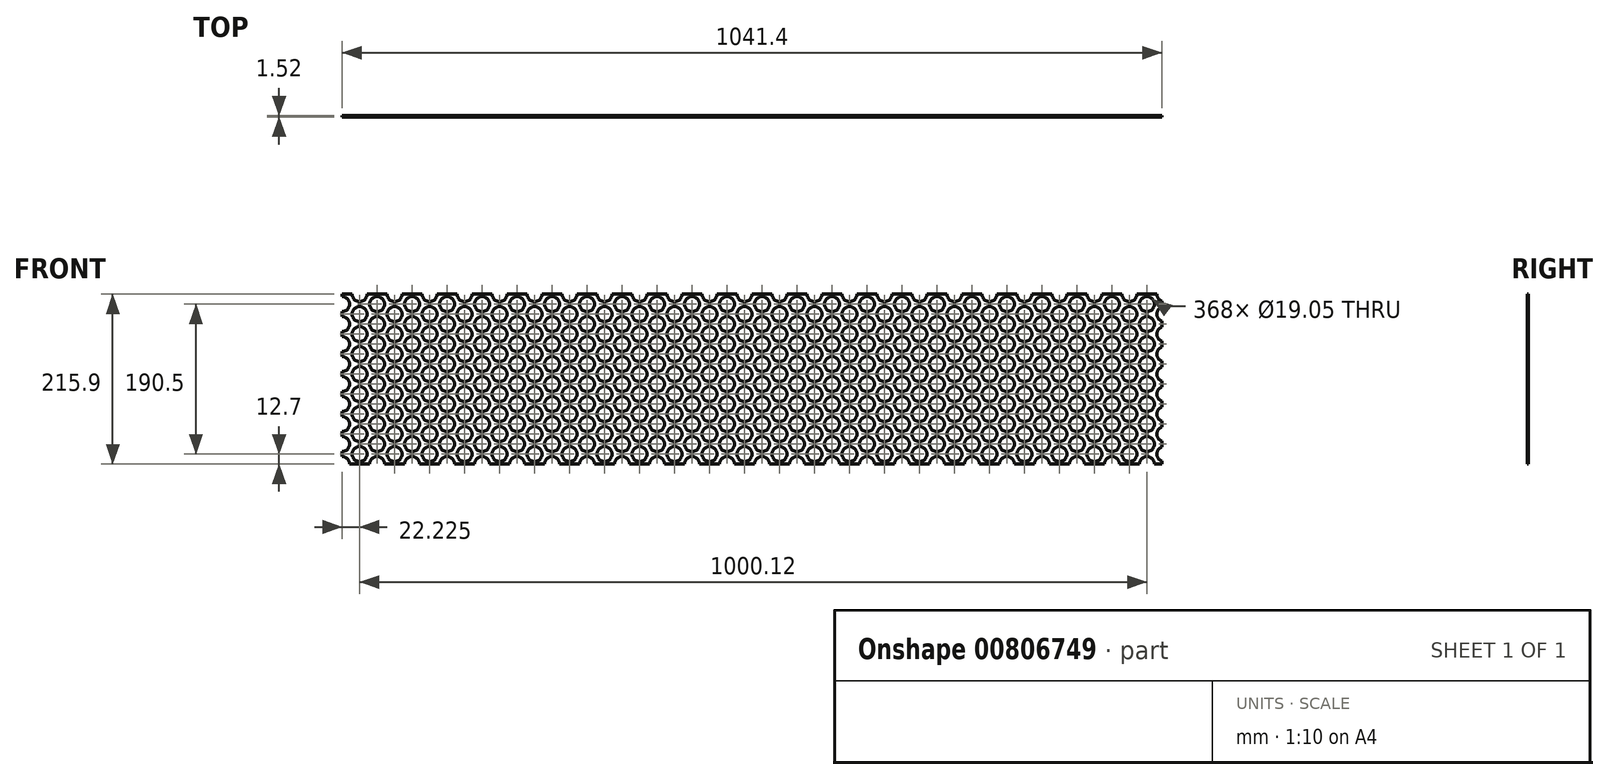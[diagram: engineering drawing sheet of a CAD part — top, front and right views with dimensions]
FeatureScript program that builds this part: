
annotation { "Feature Type Name" : "Feature", "Feature Type Description" : "" }
export const myFeature = defineFeature(function(context is Context, id is Id, definition is map)
    precondition{}
    {
        {
            var Q0;
            Q0=qCreatedBy(makeId("Front.planeOp"),FACE);
            var sketch = newSketch(context, id + "F0", { "sketchPlane" : qUnion([Q0])});
            skLineSegment(sketch, "E0.bottom", {"start": v(0, 0) * mm, "end": v(1041.4, 0) * mm});
            skLineSegment(sketch, "E0.top", {"start": v(0, 215.9) * mm, "end": v(1041.4, 215.9) * mm});
            skLineSegment(sketch, "E0.left", {"start": v(0, 0) * mm, "end": v(0, 215.9) * mm});
            skLineSegment(sketch, "E0.right", {"start": v(1041.4, 0) * mm, "end": v(1041.4, 215.9) * mm});
            skSolve(sketch);
        }
        {
            var Q0;
            Q0 = qSketchRegion(id + "F0", true);
            extrude(context, id + "F1", {"entities" : qUnion([Q0]), "depth" : 1.52 * mm, "offsetDistance" : 25.4 * mm});
        }
        {
            var Q0;
            Q0=makeQuery(id+"F1.opExtrude","CAP_FACE",FACE,{"disambiguationData":[OSD([sQuery(id+"F0.wireOp",EDGE,"E0.bottom"),sQuery(id+"F0.wireOp",EDGE,"E0.top"),sQuery(id+"F0.wireOp",EDGE,"E0.left"),sQuery(id+"F0.wireOp",EDGE,"E0.right")])],"isStart":false});
            var sketch = newSketch(context, id + "F2", { "sketchPlane" : qUnion([Q0])});
            skCircle(sketch, "E1", {"center": v(0, 0) * mm, "radius": 9.53 * mm});
            skCircle(sketch, "E2.0.1.0", {"center": v(0, 25.4) * mm, "radius": 9.53 * mm});
            skCircle(sketch, "E2.0.2.0", {"center": v(0, 50.8) * mm, "radius": 9.53 * mm});
            skCircle(sketch, "E2.0.3.0", {"center": v(0, 76.2) * mm, "radius": 9.53 * mm});
            skCircle(sketch, "E2.0.4.0", {"center": v(0, 101.6) * mm, "radius": 9.53 * mm});
            skCircle(sketch, "E2.0.5.0", {"center": v(0, 127) * mm, "radius": 9.53 * mm});
            skCircle(sketch, "E2.0.6.0", {"center": v(0, 152.4) * mm, "radius": 9.53 * mm});
            skCircle(sketch, "E2.0.7.0", {"center": v(0, 177.8) * mm, "radius": 9.53 * mm});
            skCircle(sketch, "E2.0.8.0", {"center": v(0, 203.2) * mm, "radius": 9.53 * mm});
            skCircle(sketch, "E2.1.0.0", {"center": v(44.45, 0) * mm, "radius": 9.53 * mm});
            skCircle(sketch, "E2.1.1.0", {"center": v(44.45, 25.4) * mm, "radius": 9.53 * mm});
            skCircle(sketch, "E2.1.2.0", {"center": v(44.45, 50.8) * mm, "radius": 9.53 * mm});
            skCircle(sketch, "E2.1.3.0", {"center": v(44.45, 76.2) * mm, "radius": 9.53 * mm});
            skCircle(sketch, "E2.1.4.0", {"center": v(44.45, 101.6) * mm, "radius": 9.53 * mm});
            skCircle(sketch, "E2.1.5.0", {"center": v(44.45, 127) * mm, "radius": 9.53 * mm});
            skCircle(sketch, "E2.1.6.0", {"center": v(44.45, 152.4) * mm, "radius": 9.53 * mm});
            skCircle(sketch, "E2.1.7.0", {"center": v(44.45, 177.8) * mm, "radius": 9.53 * mm});
            skCircle(sketch, "E2.1.8.0", {"center": v(44.45, 203.2) * mm, "radius": 9.53 * mm});
            skCircle(sketch, "E2.2.0.0", {"center": v(88.9, 0) * mm, "radius": 9.53 * mm});
            skCircle(sketch, "E2.2.1.0", {"center": v(88.9, 25.4) * mm, "radius": 9.53 * mm});
            skCircle(sketch, "E2.2.2.0", {"center": v(88.9, 50.8) * mm, "radius": 9.53 * mm});
            skCircle(sketch, "E2.2.3.0", {"center": v(88.9, 76.2) * mm, "radius": 9.53 * mm});
            skCircle(sketch, "E2.2.4.0", {"center": v(88.9, 101.6) * mm, "radius": 9.53 * mm});
            skCircle(sketch, "E2.2.5.0", {"center": v(88.9, 127) * mm, "radius": 9.53 * mm});
            skCircle(sketch, "E2.2.6.0", {"center": v(88.9, 152.4) * mm, "radius": 9.53 * mm});
            skCircle(sketch, "E2.2.7.0", {"center": v(88.9, 177.8) * mm, "radius": 9.53 * mm});
            skCircle(sketch, "E2.2.8.0", {"center": v(88.9, 203.2) * mm, "radius": 9.53 * mm});
            skCircle(sketch, "E2.3.0.0", {"center": v(133.35, 0) * mm, "radius": 9.53 * mm});
            skCircle(sketch, "E2.3.1.0", {"center": v(133.35, 25.4) * mm, "radius": 9.53 * mm});
            skCircle(sketch, "E2.3.2.0", {"center": v(133.35, 50.8) * mm, "radius": 9.53 * mm});
            skCircle(sketch, "E2.3.3.0", {"center": v(133.35, 76.2) * mm, "radius": 9.53 * mm});
            skCircle(sketch, "E2.3.4.0", {"center": v(133.35, 101.6) * mm, "radius": 9.53 * mm});
            skCircle(sketch, "E2.3.5.0", {"center": v(133.35, 127) * mm, "radius": 9.53 * mm});
            skCircle(sketch, "E2.3.6.0", {"center": v(133.35, 152.4) * mm, "radius": 9.53 * mm});
            skCircle(sketch, "E2.3.7.0", {"center": v(133.35, 177.8) * mm, "radius": 9.53 * mm});
            skCircle(sketch, "E2.3.8.0", {"center": v(133.35, 203.2) * mm, "radius": 9.53 * mm});
            skCircle(sketch, "E2.4.0.0", {"center": v(177.8, 0) * mm, "radius": 9.53 * mm});
            skCircle(sketch, "E2.4.1.0", {"center": v(177.8, 25.4) * mm, "radius": 9.53 * mm});
            skCircle(sketch, "E2.4.2.0", {"center": v(177.8, 50.8) * mm, "radius": 9.53 * mm});
            skCircle(sketch, "E2.4.3.0", {"center": v(177.8, 76.2) * mm, "radius": 9.53 * mm});
            skCircle(sketch, "E2.4.4.0", {"center": v(177.8, 101.6) * mm, "radius": 9.53 * mm});
            skCircle(sketch, "E2.4.5.0", {"center": v(177.8, 127) * mm, "radius": 9.53 * mm});
            skCircle(sketch, "E2.4.6.0", {"center": v(177.8, 152.4) * mm, "radius": 9.53 * mm});
            skCircle(sketch, "E2.4.7.0", {"center": v(177.8, 177.8) * mm, "radius": 9.53 * mm});
            skCircle(sketch, "E2.4.8.0", {"center": v(177.8, 203.2) * mm, "radius": 9.53 * mm});
            skCircle(sketch, "E2.5.0.0", {"center": v(222.25, 0) * mm, "radius": 9.53 * mm});
            skCircle(sketch, "E2.5.1.0", {"center": v(222.25, 25.4) * mm, "radius": 9.53 * mm});
            skCircle(sketch, "E2.5.2.0", {"center": v(222.25, 50.8) * mm, "radius": 9.53 * mm});
            skCircle(sketch, "E2.5.3.0", {"center": v(222.25, 76.2) * mm, "radius": 9.53 * mm});
            skCircle(sketch, "E2.5.4.0", {"center": v(222.25, 101.6) * mm, "radius": 9.53 * mm});
            skCircle(sketch, "E2.5.5.0", {"center": v(222.25, 127) * mm, "radius": 9.53 * mm});
            skCircle(sketch, "E2.5.6.0", {"center": v(222.25, 152.4) * mm, "radius": 9.53 * mm});
            skCircle(sketch, "E2.5.7.0", {"center": v(222.25, 177.8) * mm, "radius": 9.53 * mm});
            skCircle(sketch, "E2.5.8.0", {"center": v(222.25, 203.2) * mm, "radius": 9.53 * mm});
            skCircle(sketch, "E2.6.0.0", {"center": v(266.7, 0) * mm, "radius": 9.53 * mm});
            skCircle(sketch, "E2.6.1.0", {"center": v(266.7, 25.4) * mm, "radius": 9.53 * mm});
            skCircle(sketch, "E2.6.2.0", {"center": v(266.7, 50.8) * mm, "radius": 9.53 * mm});
            skCircle(sketch, "E2.6.3.0", {"center": v(266.7, 76.2) * mm, "radius": 9.53 * mm});
            skCircle(sketch, "E2.6.4.0", {"center": v(266.7, 101.6) * mm, "radius": 9.53 * mm});
            skCircle(sketch, "E2.6.5.0", {"center": v(266.7, 127) * mm, "radius": 9.53 * mm});
            skCircle(sketch, "E2.6.6.0", {"center": v(266.7, 152.4) * mm, "radius": 9.53 * mm});
            skCircle(sketch, "E2.6.7.0", {"center": v(266.7, 177.8) * mm, "radius": 9.53 * mm});
            skCircle(sketch, "E2.6.8.0", {"center": v(266.7, 203.2) * mm, "radius": 9.53 * mm});
            skCircle(sketch, "E2.7.0.0", {"center": v(311.15, 0) * mm, "radius": 9.53 * mm});
            skCircle(sketch, "E2.7.1.0", {"center": v(311.15, 25.4) * mm, "radius": 9.53 * mm});
            skCircle(sketch, "E2.7.2.0", {"center": v(311.15, 50.8) * mm, "radius": 9.53 * mm});
            skCircle(sketch, "E2.7.3.0", {"center": v(311.15, 76.2) * mm, "radius": 9.53 * mm});
            skCircle(sketch, "E2.7.4.0", {"center": v(311.15, 101.6) * mm, "radius": 9.53 * mm});
            skCircle(sketch, "E2.7.5.0", {"center": v(311.15, 127) * mm, "radius": 9.53 * mm});
            skCircle(sketch, "E2.7.6.0", {"center": v(311.15, 152.4) * mm, "radius": 9.53 * mm});
            skCircle(sketch, "E2.7.7.0", {"center": v(311.15, 177.8) * mm, "radius": 9.53 * mm});
            skCircle(sketch, "E2.7.8.0", {"center": v(311.15, 203.2) * mm, "radius": 9.53 * mm});
            skCircle(sketch, "E2.8.0.0", {"center": v(355.6, 0) * mm, "radius": 9.53 * mm});
            skCircle(sketch, "E2.8.1.0", {"center": v(355.6, 25.4) * mm, "radius": 9.53 * mm});
            skCircle(sketch, "E2.8.2.0", {"center": v(355.6, 50.8) * mm, "radius": 9.53 * mm});
            skCircle(sketch, "E2.8.3.0", {"center": v(355.6, 76.2) * mm, "radius": 9.53 * mm});
            skCircle(sketch, "E2.8.4.0", {"center": v(355.6, 101.6) * mm, "radius": 9.53 * mm});
            skCircle(sketch, "E2.8.5.0", {"center": v(355.6, 127) * mm, "radius": 9.53 * mm});
            skCircle(sketch, "E2.8.6.0", {"center": v(355.6, 152.4) * mm, "radius": 9.53 * mm});
            skCircle(sketch, "E2.8.7.0", {"center": v(355.6, 177.8) * mm, "radius": 9.53 * mm});
            skCircle(sketch, "E2.8.8.0", {"center": v(355.6, 203.2) * mm, "radius": 9.53 * mm});
            skCircle(sketch, "E2.9.0.0", {"center": v(400.05, 0) * mm, "radius": 9.53 * mm});
            skCircle(sketch, "E2.9.1.0", {"center": v(400.05, 25.4) * mm, "radius": 9.53 * mm});
            skCircle(sketch, "E2.9.2.0", {"center": v(400.05, 50.8) * mm, "radius": 9.53 * mm});
            skCircle(sketch, "E2.9.3.0", {"center": v(400.05, 76.2) * mm, "radius": 9.53 * mm});
            skCircle(sketch, "E2.9.4.0", {"center": v(400.05, 101.6) * mm, "radius": 9.53 * mm});
            skCircle(sketch, "E2.9.5.0", {"center": v(400.05, 127) * mm, "radius": 9.53 * mm});
            skCircle(sketch, "E2.9.6.0", {"center": v(400.05, 152.4) * mm, "radius": 9.53 * mm});
            skCircle(sketch, "E2.9.7.0", {"center": v(400.05, 177.8) * mm, "radius": 9.53 * mm});
            skCircle(sketch, "E2.9.8.0", {"center": v(400.05, 203.2) * mm, "radius": 9.53 * mm});
            skCircle(sketch, "E2.10.0.0", {"center": v(444.5, 0) * mm, "radius": 9.53 * mm});
            skCircle(sketch, "E2.10.1.0", {"center": v(444.5, 25.4) * mm, "radius": 9.53 * mm});
            skCircle(sketch, "E2.10.2.0", {"center": v(444.5, 50.8) * mm, "radius": 9.53 * mm});
            skCircle(sketch, "E2.10.3.0", {"center": v(444.5, 76.2) * mm, "radius": 9.53 * mm});
            skCircle(sketch, "E2.10.4.0", {"center": v(444.5, 101.6) * mm, "radius": 9.53 * mm});
            skCircle(sketch, "E2.10.5.0", {"center": v(444.5, 127) * mm, "radius": 9.53 * mm});
            skCircle(sketch, "E2.10.6.0", {"center": v(444.5, 152.4) * mm, "radius": 9.53 * mm});
            skCircle(sketch, "E2.10.7.0", {"center": v(444.5, 177.8) * mm, "radius": 9.53 * mm});
            skCircle(sketch, "E2.10.8.0", {"center": v(444.5, 203.2) * mm, "radius": 9.53 * mm});
            skCircle(sketch, "E2.11.0.0", {"center": v(488.95, 0) * mm, "radius": 9.53 * mm});
            skCircle(sketch, "E2.11.1.0", {"center": v(488.95, 25.4) * mm, "radius": 9.53 * mm});
            skCircle(sketch, "E2.11.2.0", {"center": v(488.95, 50.8) * mm, "radius": 9.53 * mm});
            skCircle(sketch, "E2.11.3.0", {"center": v(488.95, 76.2) * mm, "radius": 9.53 * mm});
            skCircle(sketch, "E2.11.4.0", {"center": v(488.95, 101.6) * mm, "radius": 9.53 * mm});
            skCircle(sketch, "E2.11.5.0", {"center": v(488.95, 127) * mm, "radius": 9.53 * mm});
            skCircle(sketch, "E2.11.6.0", {"center": v(488.95, 152.4) * mm, "radius": 9.53 * mm});
            skCircle(sketch, "E2.11.7.0", {"center": v(488.95, 177.8) * mm, "radius": 9.53 * mm});
            skCircle(sketch, "E2.11.8.0", {"center": v(488.95, 203.2) * mm, "radius": 9.53 * mm});
            skCircle(sketch, "E2.12.0.0", {"center": v(533.4, 0) * mm, "radius": 9.53 * mm});
            skCircle(sketch, "E2.12.1.0", {"center": v(533.4, 25.4) * mm, "radius": 9.53 * mm});
            skCircle(sketch, "E2.12.2.0", {"center": v(533.4, 50.8) * mm, "radius": 9.53 * mm});
            skCircle(sketch, "E2.12.3.0", {"center": v(533.4, 76.2) * mm, "radius": 9.53 * mm});
            skCircle(sketch, "E2.12.4.0", {"center": v(533.4, 101.6) * mm, "radius": 9.53 * mm});
            skCircle(sketch, "E2.12.5.0", {"center": v(533.4, 127) * mm, "radius": 9.53 * mm});
            skCircle(sketch, "E2.12.6.0", {"center": v(533.4, 152.4) * mm, "radius": 9.53 * mm});
            skCircle(sketch, "E2.12.7.0", {"center": v(533.4, 177.8) * mm, "radius": 9.53 * mm});
            skCircle(sketch, "E2.12.8.0", {"center": v(533.4, 203.2) * mm, "radius": 9.53 * mm});
            skCircle(sketch, "E2.13.0.0", {"center": v(577.85, 0) * mm, "radius": 9.53 * mm});
            skCircle(sketch, "E2.13.1.0", {"center": v(577.85, 25.4) * mm, "radius": 9.53 * mm});
            skCircle(sketch, "E2.13.2.0", {"center": v(577.85, 50.8) * mm, "radius": 9.53 * mm});
            skCircle(sketch, "E2.13.3.0", {"center": v(577.85, 76.2) * mm, "radius": 9.53 * mm});
            skCircle(sketch, "E2.13.4.0", {"center": v(577.85, 101.6) * mm, "radius": 9.53 * mm});
            skCircle(sketch, "E2.13.5.0", {"center": v(577.85, 127) * mm, "radius": 9.53 * mm});
            skCircle(sketch, "E2.13.6.0", {"center": v(577.85, 152.4) * mm, "radius": 9.53 * mm});
            skCircle(sketch, "E2.13.7.0", {"center": v(577.85, 177.8) * mm, "radius": 9.53 * mm});
            skCircle(sketch, "E2.13.8.0", {"center": v(577.85, 203.2) * mm, "radius": 9.53 * mm});
            skCircle(sketch, "E2.14.0.0", {"center": v(622.3, 0) * mm, "radius": 9.53 * mm});
            skCircle(sketch, "E2.14.1.0", {"center": v(622.3, 25.4) * mm, "radius": 9.53 * mm});
            skCircle(sketch, "E2.14.2.0", {"center": v(622.3, 50.8) * mm, "radius": 9.53 * mm});
            skCircle(sketch, "E2.14.3.0", {"center": v(622.3, 76.2) * mm, "radius": 9.53 * mm});
            skCircle(sketch, "E2.14.4.0", {"center": v(622.3, 101.6) * mm, "radius": 9.53 * mm});
            skCircle(sketch, "E2.14.5.0", {"center": v(622.3, 127) * mm, "radius": 9.53 * mm});
            skCircle(sketch, "E2.14.6.0", {"center": v(622.3, 152.4) * mm, "radius": 9.53 * mm});
            skCircle(sketch, "E2.14.7.0", {"center": v(622.3, 177.8) * mm, "radius": 9.53 * mm});
            skCircle(sketch, "E2.14.8.0", {"center": v(622.3, 203.2) * mm, "radius": 9.53 * mm});
            skCircle(sketch, "E2.15.0.0", {"center": v(666.75, 0) * mm, "radius": 9.53 * mm});
            skCircle(sketch, "E2.15.1.0", {"center": v(666.75, 25.4) * mm, "radius": 9.53 * mm});
            skCircle(sketch, "E2.15.2.0", {"center": v(666.75, 50.8) * mm, "radius": 9.53 * mm});
            skCircle(sketch, "E2.15.3.0", {"center": v(666.75, 76.2) * mm, "radius": 9.53 * mm});
            skCircle(sketch, "E2.15.4.0", {"center": v(666.75, 101.6) * mm, "radius": 9.53 * mm});
            skCircle(sketch, "E2.15.5.0", {"center": v(666.75, 127) * mm, "radius": 9.53 * mm});
            skCircle(sketch, "E2.15.6.0", {"center": v(666.75, 152.4) * mm, "radius": 9.53 * mm});
            skCircle(sketch, "E2.15.7.0", {"center": v(666.75, 177.8) * mm, "radius": 9.53 * mm});
            skCircle(sketch, "E2.15.8.0", {"center": v(666.75, 203.2) * mm, "radius": 9.53 * mm});
            skCircle(sketch, "E2.16.0.0", {"center": v(711.2, 0) * mm, "radius": 9.53 * mm});
            skCircle(sketch, "E2.16.1.0", {"center": v(711.2, 25.4) * mm, "radius": 9.53 * mm});
            skCircle(sketch, "E2.16.2.0", {"center": v(711.2, 50.8) * mm, "radius": 9.53 * mm});
            skCircle(sketch, "E2.16.3.0", {"center": v(711.2, 76.2) * mm, "radius": 9.53 * mm});
            skCircle(sketch, "E2.16.4.0", {"center": v(711.2, 101.6) * mm, "radius": 9.53 * mm});
            skCircle(sketch, "E2.16.5.0", {"center": v(711.2, 127) * mm, "radius": 9.53 * mm});
            skCircle(sketch, "E2.16.6.0", {"center": v(711.2, 152.4) * mm, "radius": 9.53 * mm});
            skCircle(sketch, "E2.16.7.0", {"center": v(711.2, 177.8) * mm, "radius": 9.53 * mm});
            skCircle(sketch, "E2.16.8.0", {"center": v(711.2, 203.2) * mm, "radius": 9.53 * mm});
            skCircle(sketch, "E2.17.0.0", {"center": v(755.65, 0) * mm, "radius": 9.53 * mm});
            skCircle(sketch, "E2.17.1.0", {"center": v(755.65, 25.4) * mm, "radius": 9.53 * mm});
            skCircle(sketch, "E2.17.2.0", {"center": v(755.65, 50.8) * mm, "radius": 9.53 * mm});
            skCircle(sketch, "E2.17.3.0", {"center": v(755.65, 76.2) * mm, "radius": 9.53 * mm});
            skCircle(sketch, "E2.17.4.0", {"center": v(755.65, 101.6) * mm, "radius": 9.53 * mm});
            skCircle(sketch, "E2.17.5.0", {"center": v(755.65, 127) * mm, "radius": 9.53 * mm});
            skCircle(sketch, "E2.17.6.0", {"center": v(755.65, 152.4) * mm, "radius": 9.53 * mm});
            skCircle(sketch, "E2.17.7.0", {"center": v(755.65, 177.8) * mm, "radius": 9.53 * mm});
            skCircle(sketch, "E2.17.8.0", {"center": v(755.65, 203.2) * mm, "radius": 9.53 * mm});
            skCircle(sketch, "E2.18.0.0", {"center": v(800.1, 0) * mm, "radius": 9.53 * mm});
            skCircle(sketch, "E2.18.1.0", {"center": v(800.1, 25.4) * mm, "radius": 9.53 * mm});
            skCircle(sketch, "E2.18.2.0", {"center": v(800.1, 50.8) * mm, "radius": 9.53 * mm});
            skCircle(sketch, "E2.18.3.0", {"center": v(800.1, 76.2) * mm, "radius": 9.53 * mm});
            skCircle(sketch, "E2.18.4.0", {"center": v(800.1, 101.6) * mm, "radius": 9.53 * mm});
            skCircle(sketch, "E2.18.5.0", {"center": v(800.1, 127) * mm, "radius": 9.53 * mm});
            skCircle(sketch, "E2.18.6.0", {"center": v(800.1, 152.4) * mm, "radius": 9.53 * mm});
            skCircle(sketch, "E2.18.7.0", {"center": v(800.1, 177.8) * mm, "radius": 9.53 * mm});
            skCircle(sketch, "E2.18.8.0", {"center": v(800.1, 203.2) * mm, "radius": 9.53 * mm});
            skCircle(sketch, "E2.19.0.0", {"center": v(844.55, 0) * mm, "radius": 9.53 * mm});
            skCircle(sketch, "E2.19.1.0", {"center": v(844.55, 25.4) * mm, "radius": 9.53 * mm});
            skCircle(sketch, "E2.19.2.0", {"center": v(844.55, 50.8) * mm, "radius": 9.53 * mm});
            skCircle(sketch, "E2.19.3.0", {"center": v(844.55, 76.2) * mm, "radius": 9.53 * mm});
            skCircle(sketch, "E2.19.4.0", {"center": v(844.55, 101.6) * mm, "radius": 9.53 * mm});
            skCircle(sketch, "E2.19.5.0", {"center": v(844.55, 127) * mm, "radius": 9.53 * mm});
            skCircle(sketch, "E2.19.6.0", {"center": v(844.55, 152.4) * mm, "radius": 9.53 * mm});
            skCircle(sketch, "E2.19.7.0", {"center": v(844.55, 177.8) * mm, "radius": 9.53 * mm});
            skCircle(sketch, "E2.19.8.0", {"center": v(844.55, 203.2) * mm, "radius": 9.53 * mm});
            skCircle(sketch, "E2.20.0.0", {"center": v(889, 0) * mm, "radius": 9.53 * mm});
            skCircle(sketch, "E2.20.1.0", {"center": v(889, 25.4) * mm, "radius": 9.53 * mm});
            skCircle(sketch, "E2.20.2.0", {"center": v(889, 50.8) * mm, "radius": 9.53 * mm});
            skCircle(sketch, "E2.20.3.0", {"center": v(889, 76.2) * mm, "radius": 9.53 * mm});
            skCircle(sketch, "E2.20.4.0", {"center": v(889, 101.6) * mm, "radius": 9.53 * mm});
            skCircle(sketch, "E2.20.5.0", {"center": v(889, 127) * mm, "radius": 9.53 * mm});
            skCircle(sketch, "E2.20.6.0", {"center": v(889, 152.4) * mm, "radius": 9.53 * mm});
            skCircle(sketch, "E2.20.7.0", {"center": v(889, 177.8) * mm, "radius": 9.53 * mm});
            skCircle(sketch, "E2.20.8.0", {"center": v(889, 203.2) * mm, "radius": 9.53 * mm});
            skCircle(sketch, "E2.21.0.0", {"center": v(933.45, 0) * mm, "radius": 9.53 * mm});
            skCircle(sketch, "E2.21.1.0", {"center": v(933.45, 25.4) * mm, "radius": 9.53 * mm});
            skCircle(sketch, "E2.21.2.0", {"center": v(933.45, 50.8) * mm, "radius": 9.53 * mm});
            skCircle(sketch, "E2.21.3.0", {"center": v(933.45, 76.2) * mm, "radius": 9.53 * mm});
            skCircle(sketch, "E2.21.4.0", {"center": v(933.45, 101.6) * mm, "radius": 9.53 * mm});
            skCircle(sketch, "E2.21.5.0", {"center": v(933.45, 127) * mm, "radius": 9.53 * mm});
            skCircle(sketch, "E2.21.6.0", {"center": v(933.45, 152.4) * mm, "radius": 9.53 * mm});
            skCircle(sketch, "E2.21.7.0", {"center": v(933.45, 177.8) * mm, "radius": 9.53 * mm});
            skCircle(sketch, "E2.21.8.0", {"center": v(933.45, 203.2) * mm, "radius": 9.53 * mm});
            skCircle(sketch, "E2.22.0.0", {"center": v(977.9, 0) * mm, "radius": 9.53 * mm});
            skCircle(sketch, "E2.22.1.0", {"center": v(977.9, 25.4) * mm, "radius": 9.53 * mm});
            skCircle(sketch, "E2.22.2.0", {"center": v(977.9, 50.8) * mm, "radius": 9.53 * mm});
            skCircle(sketch, "E2.22.3.0", {"center": v(977.9, 76.2) * mm, "radius": 9.53 * mm});
            skCircle(sketch, "E2.22.4.0", {"center": v(977.9, 101.6) * mm, "radius": 9.53 * mm});
            skCircle(sketch, "E2.22.5.0", {"center": v(977.9, 127) * mm, "radius": 9.53 * mm});
            skCircle(sketch, "E2.22.6.0", {"center": v(977.9, 152.4) * mm, "radius": 9.53 * mm});
            skCircle(sketch, "E2.22.7.0", {"center": v(977.9, 177.8) * mm, "radius": 9.53 * mm});
            skCircle(sketch, "E2.22.8.0", {"center": v(977.9, 203.2) * mm, "radius": 9.53 * mm});
            skCircle(sketch, "E2.23.0.0", {"center": v(1022.35, 0) * mm, "radius": 9.53 * mm});
            skCircle(sketch, "E2.23.1.0", {"center": v(1022.35, 25.4) * mm, "radius": 9.53 * mm});
            skCircle(sketch, "E2.23.2.0", {"center": v(1022.35, 50.8) * mm, "radius": 9.53 * mm});
            skCircle(sketch, "E2.23.3.0", {"center": v(1022.35, 76.2) * mm, "radius": 9.53 * mm});
            skCircle(sketch, "E2.23.4.0", {"center": v(1022.35, 101.6) * mm, "radius": 9.53 * mm});
            skCircle(sketch, "E2.23.5.0", {"center": v(1022.35, 127) * mm, "radius": 9.53 * mm});
            skCircle(sketch, "E2.23.6.0", {"center": v(1022.35, 152.4) * mm, "radius": 9.53 * mm});
            skCircle(sketch, "E2.23.7.0", {"center": v(1022.35, 177.8) * mm, "radius": 9.53 * mm});
            skCircle(sketch, "E2.23.8.0", {"center": v(1022.35, 203.2) * mm, "radius": 9.53 * mm});
            skLineSegment(sketch, "E2.direction1", {"start": v(0, 0) * mm, "end": v(44.45, 0) * mm, "construction": true});
            skLineSegment(sketch, "E2.direction2", {"start": v(0, 0) * mm, "end": v(0, 25.4) * mm, "construction": true});
            skCircle(sketch, "E3", {"center": v(22.22, 12.7) * mm, "radius": 9.53 * mm});
            skCircle(sketch, "E4.0.1.0", {"center": v(22.22, 38.1) * mm, "radius": 9.53 * mm});
            skCircle(sketch, "E4.0.2.0", {"center": v(22.22, 63.5) * mm, "radius": 9.53 * mm});
            skCircle(sketch, "E4.0.3.0", {"center": v(22.22, 88.9) * mm, "radius": 9.53 * mm});
            skCircle(sketch, "E4.0.4.0", {"center": v(22.22, 114.3) * mm, "radius": 9.53 * mm});
            skCircle(sketch, "E4.0.5.0", {"center": v(22.22, 139.7) * mm, "radius": 9.53 * mm});
            skCircle(sketch, "E4.0.6.0", {"center": v(22.22, 165.1) * mm, "radius": 9.53 * mm});
            skCircle(sketch, "E4.0.7.0", {"center": v(22.22, 190.5) * mm, "radius": 9.53 * mm});
            skCircle(sketch, "E4.0.8.0", {"center": v(22.22, 215.9) * mm, "radius": 9.53 * mm});
            skCircle(sketch, "E4.1.0.0", {"center": v(66.67, 12.7) * mm, "radius": 9.53 * mm});
            skCircle(sketch, "E4.1.1.0", {"center": v(66.67, 38.1) * mm, "radius": 9.53 * mm});
            skCircle(sketch, "E4.1.2.0", {"center": v(66.67, 63.5) * mm, "radius": 9.53 * mm});
            skCircle(sketch, "E4.1.3.0", {"center": v(66.67, 88.9) * mm, "radius": 9.53 * mm});
            skCircle(sketch, "E4.1.4.0", {"center": v(66.67, 114.3) * mm, "radius": 9.53 * mm});
            skCircle(sketch, "E4.1.5.0", {"center": v(66.67, 139.7) * mm, "radius": 9.53 * mm});
            skCircle(sketch, "E4.1.6.0", {"center": v(66.67, 165.1) * mm, "radius": 9.53 * mm});
            skCircle(sketch, "E4.1.7.0", {"center": v(66.67, 190.5) * mm, "radius": 9.53 * mm});
            skCircle(sketch, "E4.1.8.0", {"center": v(66.67, 215.9) * mm, "radius": 9.53 * mm});
            skCircle(sketch, "E4.2.0.0", {"center": v(111.12, 12.7) * mm, "radius": 9.53 * mm});
            skCircle(sketch, "E4.2.1.0", {"center": v(111.12, 38.1) * mm, "radius": 9.53 * mm});
            skCircle(sketch, "E4.2.2.0", {"center": v(111.12, 63.5) * mm, "radius": 9.53 * mm});
            skCircle(sketch, "E4.2.3.0", {"center": v(111.12, 88.9) * mm, "radius": 9.53 * mm});
            skCircle(sketch, "E4.2.4.0", {"center": v(111.12, 114.3) * mm, "radius": 9.53 * mm});
            skCircle(sketch, "E4.2.5.0", {"center": v(111.12, 139.7) * mm, "radius": 9.53 * mm});
            skCircle(sketch, "E4.2.6.0", {"center": v(111.12, 165.1) * mm, "radius": 9.53 * mm});
            skCircle(sketch, "E4.2.7.0", {"center": v(111.12, 190.5) * mm, "radius": 9.53 * mm});
            skCircle(sketch, "E4.2.8.0", {"center": v(111.12, 215.9) * mm, "radius": 9.53 * mm});
            skCircle(sketch, "E4.3.0.0", {"center": v(155.58, 12.7) * mm, "radius": 9.53 * mm});
            skCircle(sketch, "E4.3.1.0", {"center": v(155.58, 38.1) * mm, "radius": 9.53 * mm});
            skCircle(sketch, "E4.3.2.0", {"center": v(155.58, 63.5) * mm, "radius": 9.53 * mm});
            skCircle(sketch, "E4.3.3.0", {"center": v(155.58, 88.9) * mm, "radius": 9.53 * mm});
            skCircle(sketch, "E4.3.4.0", {"center": v(155.58, 114.3) * mm, "radius": 9.53 * mm});
            skCircle(sketch, "E4.3.5.0", {"center": v(155.58, 139.7) * mm, "radius": 9.53 * mm});
            skCircle(sketch, "E4.3.6.0", {"center": v(155.58, 165.1) * mm, "radius": 9.53 * mm});
            skCircle(sketch, "E4.3.7.0", {"center": v(155.58, 190.5) * mm, "radius": 9.53 * mm});
            skCircle(sketch, "E4.3.8.0", {"center": v(155.58, 215.9) * mm, "radius": 9.53 * mm});
            skCircle(sketch, "E4.4.0.0", {"center": v(200.03, 12.7) * mm, "radius": 9.53 * mm});
            skCircle(sketch, "E4.4.1.0", {"center": v(200.03, 38.1) * mm, "radius": 9.53 * mm});
            skCircle(sketch, "E4.4.2.0", {"center": v(200.03, 63.5) * mm, "radius": 9.53 * mm});
            skCircle(sketch, "E4.4.3.0", {"center": v(200.03, 88.9) * mm, "radius": 9.53 * mm});
            skCircle(sketch, "E4.4.4.0", {"center": v(200.03, 114.3) * mm, "radius": 9.53 * mm});
            skCircle(sketch, "E4.4.5.0", {"center": v(200.03, 139.7) * mm, "radius": 9.53 * mm});
            skCircle(sketch, "E4.4.6.0", {"center": v(200.03, 165.1) * mm, "radius": 9.53 * mm});
            skCircle(sketch, "E4.4.7.0", {"center": v(200.03, 190.5) * mm, "radius": 9.53 * mm});
            skCircle(sketch, "E4.4.8.0", {"center": v(200.03, 215.9) * mm, "radius": 9.53 * mm});
            skCircle(sketch, "E4.5.0.0", {"center": v(244.47, 12.7) * mm, "radius": 9.53 * mm});
            skCircle(sketch, "E4.5.1.0", {"center": v(244.47, 38.1) * mm, "radius": 9.53 * mm});
            skCircle(sketch, "E4.5.2.0", {"center": v(244.47, 63.5) * mm, "radius": 9.53 * mm});
            skCircle(sketch, "E4.5.3.0", {"center": v(244.47, 88.9) * mm, "radius": 9.53 * mm});
            skCircle(sketch, "E4.5.4.0", {"center": v(244.47, 114.3) * mm, "radius": 9.53 * mm});
            skCircle(sketch, "E4.5.5.0", {"center": v(244.47, 139.7) * mm, "radius": 9.53 * mm});
            skCircle(sketch, "E4.5.6.0", {"center": v(244.47, 165.1) * mm, "radius": 9.53 * mm});
            skCircle(sketch, "E4.5.7.0", {"center": v(244.47, 190.5) * mm, "radius": 9.53 * mm});
            skCircle(sketch, "E4.5.8.0", {"center": v(244.47, 215.9) * mm, "radius": 9.53 * mm});
            skCircle(sketch, "E4.6.0.0", {"center": v(288.93, 12.7) * mm, "radius": 9.53 * mm});
            skCircle(sketch, "E4.6.1.0", {"center": v(288.93, 38.1) * mm, "radius": 9.53 * mm});
            skCircle(sketch, "E4.6.2.0", {"center": v(288.93, 63.5) * mm, "radius": 9.53 * mm});
            skCircle(sketch, "E4.6.3.0", {"center": v(288.93, 88.9) * mm, "radius": 9.53 * mm});
            skCircle(sketch, "E4.6.4.0", {"center": v(288.93, 114.3) * mm, "radius": 9.53 * mm});
            skCircle(sketch, "E4.6.5.0", {"center": v(288.93, 139.7) * mm, "radius": 9.53 * mm});
            skCircle(sketch, "E4.6.6.0", {"center": v(288.93, 165.1) * mm, "radius": 9.53 * mm});
            skCircle(sketch, "E4.6.7.0", {"center": v(288.93, 190.5) * mm, "radius": 9.53 * mm});
            skCircle(sketch, "E4.6.8.0", {"center": v(288.93, 215.9) * mm, "radius": 9.53 * mm});
            skCircle(sketch, "E4.7.0.0", {"center": v(333.38, 12.7) * mm, "radius": 9.53 * mm});
            skCircle(sketch, "E4.7.1.0", {"center": v(333.38, 38.1) * mm, "radius": 9.53 * mm});
            skCircle(sketch, "E4.7.2.0", {"center": v(333.38, 63.5) * mm, "radius": 9.53 * mm});
            skCircle(sketch, "E4.7.3.0", {"center": v(333.38, 88.9) * mm, "radius": 9.53 * mm});
            skCircle(sketch, "E4.7.4.0", {"center": v(333.38, 114.3) * mm, "radius": 9.53 * mm});
            skCircle(sketch, "E4.7.5.0", {"center": v(333.38, 139.7) * mm, "radius": 9.53 * mm});
            skCircle(sketch, "E4.7.6.0", {"center": v(333.38, 165.1) * mm, "radius": 9.53 * mm});
            skCircle(sketch, "E4.7.7.0", {"center": v(333.38, 190.5) * mm, "radius": 9.53 * mm});
            skCircle(sketch, "E4.7.8.0", {"center": v(333.38, 215.9) * mm, "radius": 9.53 * mm});
            skCircle(sketch, "E4.8.0.0", {"center": v(377.83, 12.7) * mm, "radius": 9.53 * mm});
            skCircle(sketch, "E4.8.1.0", {"center": v(377.83, 38.1) * mm, "radius": 9.53 * mm});
            skCircle(sketch, "E4.8.2.0", {"center": v(377.83, 63.5) * mm, "radius": 9.53 * mm});
            skCircle(sketch, "E4.8.3.0", {"center": v(377.83, 88.9) * mm, "radius": 9.53 * mm});
            skCircle(sketch, "E4.8.4.0", {"center": v(377.83, 114.3) * mm, "radius": 9.53 * mm});
            skCircle(sketch, "E4.8.5.0", {"center": v(377.83, 139.7) * mm, "radius": 9.53 * mm});
            skCircle(sketch, "E4.8.6.0", {"center": v(377.83, 165.1) * mm, "radius": 9.53 * mm});
            skCircle(sketch, "E4.8.7.0", {"center": v(377.83, 190.5) * mm, "radius": 9.53 * mm});
            skCircle(sketch, "E4.8.8.0", {"center": v(377.83, 215.9) * mm, "radius": 9.53 * mm});
            skCircle(sketch, "E4.9.0.0", {"center": v(422.28, 12.7) * mm, "radius": 9.53 * mm});
            skCircle(sketch, "E4.9.1.0", {"center": v(422.28, 38.1) * mm, "radius": 9.53 * mm});
            skCircle(sketch, "E4.9.2.0", {"center": v(422.28, 63.5) * mm, "radius": 9.53 * mm});
            skCircle(sketch, "E4.9.3.0", {"center": v(422.28, 88.9) * mm, "radius": 9.53 * mm});
            skCircle(sketch, "E4.9.4.0", {"center": v(422.28, 114.3) * mm, "radius": 9.53 * mm});
            skCircle(sketch, "E4.9.5.0", {"center": v(422.28, 139.7) * mm, "radius": 9.53 * mm});
            skCircle(sketch, "E4.9.6.0", {"center": v(422.28, 165.1) * mm, "radius": 9.53 * mm});
            skCircle(sketch, "E4.9.7.0", {"center": v(422.28, 190.5) * mm, "radius": 9.53 * mm});
            skCircle(sketch, "E4.9.8.0", {"center": v(422.28, 215.9) * mm, "radius": 9.53 * mm});
            skCircle(sketch, "E4.10.0.0", {"center": v(466.73, 12.7) * mm, "radius": 9.53 * mm});
            skCircle(sketch, "E4.10.1.0", {"center": v(466.73, 38.1) * mm, "radius": 9.53 * mm});
            skCircle(sketch, "E4.10.2.0", {"center": v(466.73, 63.5) * mm, "radius": 9.53 * mm});
            skCircle(sketch, "E4.10.3.0", {"center": v(466.73, 88.9) * mm, "radius": 9.53 * mm});
            skCircle(sketch, "E4.10.4.0", {"center": v(466.73, 114.3) * mm, "radius": 9.53 * mm});
            skCircle(sketch, "E4.10.5.0", {"center": v(466.73, 139.7) * mm, "radius": 9.53 * mm});
            skCircle(sketch, "E4.10.6.0", {"center": v(466.73, 165.1) * mm, "radius": 9.53 * mm});
            skCircle(sketch, "E4.10.7.0", {"center": v(466.73, 190.5) * mm, "radius": 9.53 * mm});
            skCircle(sketch, "E4.10.8.0", {"center": v(466.73, 215.9) * mm, "radius": 9.53 * mm});
            skCircle(sketch, "E4.11.0.0", {"center": v(511.18, 12.7) * mm, "radius": 9.53 * mm});
            skCircle(sketch, "E4.11.1.0", {"center": v(511.18, 38.1) * mm, "radius": 9.53 * mm});
            skCircle(sketch, "E4.11.2.0", {"center": v(511.18, 63.5) * mm, "radius": 9.53 * mm});
            skCircle(sketch, "E4.11.3.0", {"center": v(511.18, 88.9) * mm, "radius": 9.53 * mm});
            skCircle(sketch, "E4.11.4.0", {"center": v(511.18, 114.3) * mm, "radius": 9.53 * mm});
            skCircle(sketch, "E4.11.5.0", {"center": v(511.18, 139.7) * mm, "radius": 9.53 * mm});
            skCircle(sketch, "E4.11.6.0", {"center": v(511.18, 165.1) * mm, "radius": 9.53 * mm});
            skCircle(sketch, "E4.11.7.0", {"center": v(511.18, 190.5) * mm, "radius": 9.53 * mm});
            skCircle(sketch, "E4.11.8.0", {"center": v(511.18, 215.9) * mm, "radius": 9.53 * mm});
            skCircle(sketch, "E4.12.0.0", {"center": v(555.63, 12.7) * mm, "radius": 9.53 * mm});
            skCircle(sketch, "E4.12.1.0", {"center": v(555.63, 38.1) * mm, "radius": 9.53 * mm});
            skCircle(sketch, "E4.12.2.0", {"center": v(555.63, 63.5) * mm, "radius": 9.53 * mm});
            skCircle(sketch, "E4.12.3.0", {"center": v(555.63, 88.9) * mm, "radius": 9.53 * mm});
            skCircle(sketch, "E4.12.4.0", {"center": v(555.63, 114.3) * mm, "radius": 9.53 * mm});
            skCircle(sketch, "E4.12.5.0", {"center": v(555.63, 139.7) * mm, "radius": 9.53 * mm});
            skCircle(sketch, "E4.12.6.0", {"center": v(555.63, 165.1) * mm, "radius": 9.53 * mm});
            skCircle(sketch, "E4.12.7.0", {"center": v(555.63, 190.5) * mm, "radius": 9.53 * mm});
            skCircle(sketch, "E4.12.8.0", {"center": v(555.63, 215.9) * mm, "radius": 9.53 * mm});
            skCircle(sketch, "E4.13.0.0", {"center": v(600.08, 12.7) * mm, "radius": 9.53 * mm});
            skCircle(sketch, "E4.13.1.0", {"center": v(600.08, 38.1) * mm, "radius": 9.53 * mm});
            skCircle(sketch, "E4.13.2.0", {"center": v(600.08, 63.5) * mm, "radius": 9.53 * mm});
            skCircle(sketch, "E4.13.3.0", {"center": v(600.08, 88.9) * mm, "radius": 9.53 * mm});
            skCircle(sketch, "E4.13.4.0", {"center": v(600.08, 114.3) * mm, "radius": 9.53 * mm});
            skCircle(sketch, "E4.13.5.0", {"center": v(600.08, 139.7) * mm, "radius": 9.53 * mm});
            skCircle(sketch, "E4.13.6.0", {"center": v(600.08, 165.1) * mm, "radius": 9.53 * mm});
            skCircle(sketch, "E4.13.7.0", {"center": v(600.08, 190.5) * mm, "radius": 9.53 * mm});
            skCircle(sketch, "E4.13.8.0", {"center": v(600.08, 215.9) * mm, "radius": 9.53 * mm});
            skCircle(sketch, "E4.14.0.0", {"center": v(644.53, 12.7) * mm, "radius": 9.53 * mm});
            skCircle(sketch, "E4.14.1.0", {"center": v(644.53, 38.1) * mm, "radius": 9.53 * mm});
            skCircle(sketch, "E4.14.2.0", {"center": v(644.53, 63.5) * mm, "radius": 9.53 * mm});
            skCircle(sketch, "E4.14.3.0", {"center": v(644.53, 88.9) * mm, "radius": 9.53 * mm});
            skCircle(sketch, "E4.14.4.0", {"center": v(644.53, 114.3) * mm, "radius": 9.53 * mm});
            skCircle(sketch, "E4.14.5.0", {"center": v(644.53, 139.7) * mm, "radius": 9.53 * mm});
            skCircle(sketch, "E4.14.6.0", {"center": v(644.53, 165.1) * mm, "radius": 9.53 * mm});
            skCircle(sketch, "E4.14.7.0", {"center": v(644.53, 190.5) * mm, "radius": 9.53 * mm});
            skCircle(sketch, "E4.14.8.0", {"center": v(644.53, 215.9) * mm, "radius": 9.53 * mm});
            skCircle(sketch, "E4.15.0.0", {"center": v(688.98, 12.7) * mm, "radius": 9.53 * mm});
            skCircle(sketch, "E4.15.1.0", {"center": v(688.98, 38.1) * mm, "radius": 9.53 * mm});
            skCircle(sketch, "E4.15.2.0", {"center": v(688.98, 63.5) * mm, "radius": 9.53 * mm});
            skCircle(sketch, "E4.15.3.0", {"center": v(688.98, 88.9) * mm, "radius": 9.53 * mm});
            skCircle(sketch, "E4.15.4.0", {"center": v(688.98, 114.3) * mm, "radius": 9.53 * mm});
            skCircle(sketch, "E4.15.5.0", {"center": v(688.98, 139.7) * mm, "radius": 9.53 * mm});
            skCircle(sketch, "E4.15.6.0", {"center": v(688.98, 165.1) * mm, "radius": 9.53 * mm});
            skCircle(sketch, "E4.15.7.0", {"center": v(688.98, 190.5) * mm, "radius": 9.53 * mm});
            skCircle(sketch, "E4.15.8.0", {"center": v(688.98, 215.9) * mm, "radius": 9.53 * mm});
            skCircle(sketch, "E4.16.0.0", {"center": v(733.43, 12.7) * mm, "radius": 9.53 * mm});
            skCircle(sketch, "E4.16.1.0", {"center": v(733.43, 38.1) * mm, "radius": 9.53 * mm});
            skCircle(sketch, "E4.16.2.0", {"center": v(733.43, 63.5) * mm, "radius": 9.53 * mm});
            skCircle(sketch, "E4.16.3.0", {"center": v(733.43, 88.9) * mm, "radius": 9.53 * mm});
            skCircle(sketch, "E4.16.4.0", {"center": v(733.43, 114.3) * mm, "radius": 9.53 * mm});
            skCircle(sketch, "E4.16.5.0", {"center": v(733.43, 139.7) * mm, "radius": 9.53 * mm});
            skCircle(sketch, "E4.16.6.0", {"center": v(733.43, 165.1) * mm, "radius": 9.53 * mm});
            skCircle(sketch, "E4.16.7.0", {"center": v(733.43, 190.5) * mm, "radius": 9.53 * mm});
            skCircle(sketch, "E4.16.8.0", {"center": v(733.43, 215.9) * mm, "radius": 9.53 * mm});
            skCircle(sketch, "E4.17.0.0", {"center": v(777.88, 12.7) * mm, "radius": 9.53 * mm});
            skCircle(sketch, "E4.17.1.0", {"center": v(777.88, 38.1) * mm, "radius": 9.53 * mm});
            skCircle(sketch, "E4.17.2.0", {"center": v(777.88, 63.5) * mm, "radius": 9.53 * mm});
            skCircle(sketch, "E4.17.3.0", {"center": v(777.88, 88.9) * mm, "radius": 9.53 * mm});
            skCircle(sketch, "E4.17.4.0", {"center": v(777.88, 114.3) * mm, "radius": 9.53 * mm});
            skCircle(sketch, "E4.17.5.0", {"center": v(777.88, 139.7) * mm, "radius": 9.53 * mm});
            skCircle(sketch, "E4.17.6.0", {"center": v(777.88, 165.1) * mm, "radius": 9.53 * mm});
            skCircle(sketch, "E4.17.7.0", {"center": v(777.88, 190.5) * mm, "radius": 9.53 * mm});
            skCircle(sketch, "E4.17.8.0", {"center": v(777.88, 215.9) * mm, "radius": 9.53 * mm});
            skCircle(sketch, "E4.18.0.0", {"center": v(822.33, 12.7) * mm, "radius": 9.53 * mm});
            skCircle(sketch, "E4.18.1.0", {"center": v(822.33, 38.1) * mm, "radius": 9.53 * mm});
            skCircle(sketch, "E4.18.2.0", {"center": v(822.33, 63.5) * mm, "radius": 9.53 * mm});
            skCircle(sketch, "E4.18.3.0", {"center": v(822.33, 88.9) * mm, "radius": 9.53 * mm});
            skCircle(sketch, "E4.18.4.0", {"center": v(822.33, 114.3) * mm, "radius": 9.53 * mm});
            skCircle(sketch, "E4.18.5.0", {"center": v(822.33, 139.7) * mm, "radius": 9.53 * mm});
            skCircle(sketch, "E4.18.6.0", {"center": v(822.33, 165.1) * mm, "radius": 9.53 * mm});
            skCircle(sketch, "E4.18.7.0", {"center": v(822.33, 190.5) * mm, "radius": 9.53 * mm});
            skCircle(sketch, "E4.18.8.0", {"center": v(822.33, 215.9) * mm, "radius": 9.53 * mm});
            skCircle(sketch, "E4.19.0.0", {"center": v(866.78, 12.7) * mm, "radius": 9.53 * mm});
            skCircle(sketch, "E4.19.1.0", {"center": v(866.78, 38.1) * mm, "radius": 9.53 * mm});
            skCircle(sketch, "E4.19.2.0", {"center": v(866.78, 63.5) * mm, "radius": 9.53 * mm});
            skCircle(sketch, "E4.19.3.0", {"center": v(866.78, 88.9) * mm, "radius": 9.53 * mm});
            skCircle(sketch, "E4.19.4.0", {"center": v(866.78, 114.3) * mm, "radius": 9.53 * mm});
            skCircle(sketch, "E4.19.5.0", {"center": v(866.78, 139.7) * mm, "radius": 9.53 * mm});
            skCircle(sketch, "E4.19.6.0", {"center": v(866.78, 165.1) * mm, "radius": 9.53 * mm});
            skCircle(sketch, "E4.19.7.0", {"center": v(866.78, 190.5) * mm, "radius": 9.53 * mm});
            skCircle(sketch, "E4.19.8.0", {"center": v(866.78, 215.9) * mm, "radius": 9.53 * mm});
            skCircle(sketch, "E4.20.0.0", {"center": v(911.23, 12.7) * mm, "radius": 9.53 * mm});
            skCircle(sketch, "E4.20.1.0", {"center": v(911.23, 38.1) * mm, "radius": 9.53 * mm});
            skCircle(sketch, "E4.20.2.0", {"center": v(911.23, 63.5) * mm, "radius": 9.53 * mm});
            skCircle(sketch, "E4.20.3.0", {"center": v(911.23, 88.9) * mm, "radius": 9.53 * mm});
            skCircle(sketch, "E4.20.4.0", {"center": v(911.23, 114.3) * mm, "radius": 9.53 * mm});
            skCircle(sketch, "E4.20.5.0", {"center": v(911.23, 139.7) * mm, "radius": 9.53 * mm});
            skCircle(sketch, "E4.20.6.0", {"center": v(911.23, 165.1) * mm, "radius": 9.53 * mm});
            skCircle(sketch, "E4.20.7.0", {"center": v(911.23, 190.5) * mm, "radius": 9.53 * mm});
            skCircle(sketch, "E4.20.8.0", {"center": v(911.23, 215.9) * mm, "radius": 9.53 * mm});
            skCircle(sketch, "E4.21.0.0", {"center": v(955.68, 12.7) * mm, "radius": 9.53 * mm});
            skCircle(sketch, "E4.21.1.0", {"center": v(955.68, 38.1) * mm, "radius": 9.53 * mm});
            skCircle(sketch, "E4.21.2.0", {"center": v(955.68, 63.5) * mm, "radius": 9.53 * mm});
            skCircle(sketch, "E4.21.3.0", {"center": v(955.68, 88.9) * mm, "radius": 9.53 * mm});
            skCircle(sketch, "E4.21.4.0", {"center": v(955.68, 114.3) * mm, "radius": 9.53 * mm});
            skCircle(sketch, "E4.21.5.0", {"center": v(955.68, 139.7) * mm, "radius": 9.53 * mm});
            skCircle(sketch, "E4.21.6.0", {"center": v(955.68, 165.1) * mm, "radius": 9.53 * mm});
            skCircle(sketch, "E4.21.7.0", {"center": v(955.68, 190.5) * mm, "radius": 9.53 * mm});
            skCircle(sketch, "E4.21.8.0", {"center": v(955.68, 215.9) * mm, "radius": 9.53 * mm});
            skCircle(sketch, "E4.22.0.0", {"center": v(1000.13, 12.7) * mm, "radius": 9.53 * mm});
            skCircle(sketch, "E4.22.1.0", {"center": v(1000.13, 38.1) * mm, "radius": 9.53 * mm});
            skCircle(sketch, "E4.22.2.0", {"center": v(1000.13, 63.5) * mm, "radius": 9.53 * mm});
            skCircle(sketch, "E4.22.3.0", {"center": v(1000.13, 88.9) * mm, "radius": 9.53 * mm});
            skCircle(sketch, "E4.22.4.0", {"center": v(1000.13, 114.3) * mm, "radius": 9.53 * mm});
            skCircle(sketch, "E4.22.5.0", {"center": v(1000.13, 139.7) * mm, "radius": 9.53 * mm});
            skCircle(sketch, "E4.22.6.0", {"center": v(1000.13, 165.1) * mm, "radius": 9.53 * mm});
            skCircle(sketch, "E4.22.7.0", {"center": v(1000.13, 190.5) * mm, "radius": 9.53 * mm});
            skCircle(sketch, "E4.22.8.0", {"center": v(1000.13, 215.9) * mm, "radius": 9.53 * mm});
            skCircle(sketch, "E4.23.0.0", {"center": v(1044.58, 12.7) * mm, "radius": 9.53 * mm});
            skCircle(sketch, "E4.23.1.0", {"center": v(1044.58, 38.1) * mm, "radius": 9.53 * mm});
            skCircle(sketch, "E4.23.2.0", {"center": v(1044.58, 63.5) * mm, "radius": 9.53 * mm});
            skCircle(sketch, "E4.23.3.0", {"center": v(1044.58, 88.9) * mm, "radius": 9.53 * mm});
            skCircle(sketch, "E4.23.4.0", {"center": v(1044.58, 114.3) * mm, "radius": 9.53 * mm});
            skCircle(sketch, "E4.23.5.0", {"center": v(1044.58, 139.7) * mm, "radius": 9.53 * mm});
            skCircle(sketch, "E4.23.6.0", {"center": v(1044.58, 165.1) * mm, "radius": 9.53 * mm});
            skCircle(sketch, "E4.23.7.0", {"center": v(1044.58, 190.5) * mm, "radius": 9.53 * mm});
            skCircle(sketch, "E4.23.8.0", {"center": v(1044.58, 215.9) * mm, "radius": 9.53 * mm});
            skLineSegment(sketch, "E4.direction1", {"start": v(22.22, 12.7) * mm, "end": v(66.67, 12.7) * mm, "construction": true});
            skLineSegment(sketch, "E4.direction2", {"start": v(22.22, 12.7) * mm, "end": v(22.22, 38.1) * mm, "construction": true});
            skSolve(sketch);
        }
        {
            var Q0;
            Q0 = qSketchRegion(id + "F2", true);
            extrude(context, id + "F3", {"entities" : qUnion([Q0]), "operationType" : NewBodyOperationType.REMOVE, "endBound" : BoundingType.THROUGH_ALL, "oppositeDirection" : true, "depth" : 25.4 * mm, "offsetDistance" : 25.4 * mm});
        }
    });
